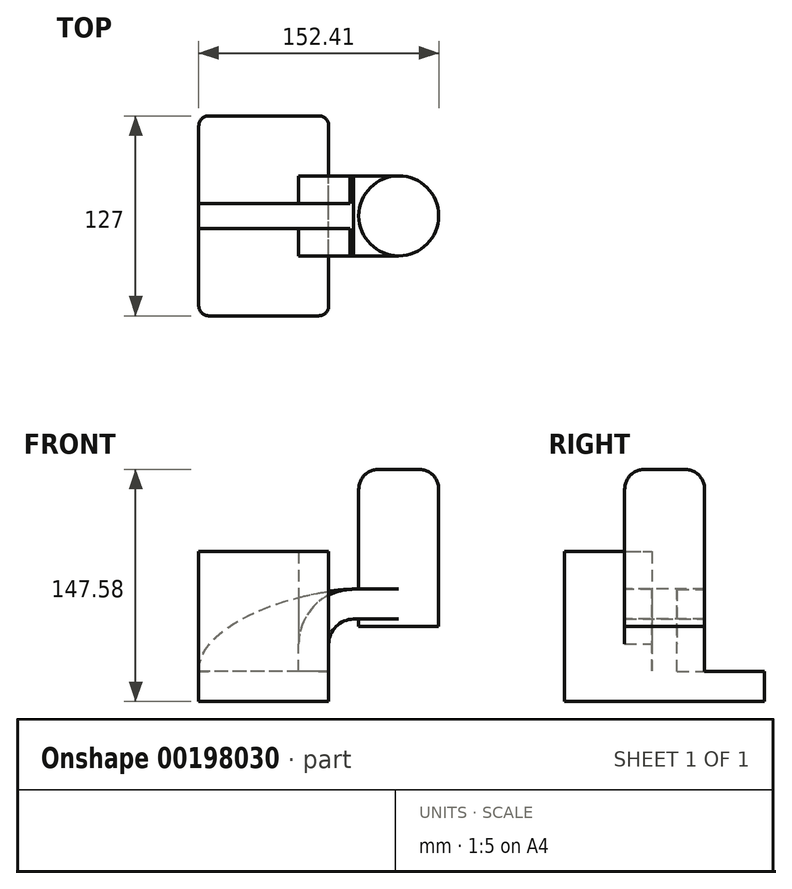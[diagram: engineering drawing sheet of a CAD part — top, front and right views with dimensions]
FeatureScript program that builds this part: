
annotation { "Feature Type Name" : "Feature", "Feature Type Description" : "" }
export const myFeature = defineFeature(function(context is Context, id is Id, definition is map)
    precondition{}
    {
        {
            var Q0;
            Q0=qCreatedBy(makeId("Front.planeOp"),FACE);
            var sketch = newSketch(context, id + "F0", { "sketchPlane" : qUnion([Q0])});
            skLineSegment(sketch, "E0.bottom", {"start": v(41.28, 9.53) * mm, "end": v(-41.28, 9.53) * mm});
            skLineSegment(sketch, "E0.top", {"start": v(41.28, -9.53) * mm, "end": v(-41.28, -9.53) * mm});
            skLineSegment(sketch, "E0.left", {"start": v(41.28, 9.53) * mm, "end": v(41.28, -9.53) * mm});
            skLineSegment(sketch, "E0.right", {"start": v(-41.28, 9.53) * mm, "end": v(-41.28, -9.53) * mm});
            skPoint(sketch, "E0.middle", {"position": v(0, 0) * mm});
            skLineSegment(sketch, "E1", {"start": v(41.28, 9.53) * mm, "end": v(41.28, 27) * mm});
            skArc(sketch, "E2", {"start": v(41.27, 27) * mm, "mid": v(45.92, 38.23) * mm, "end": v(57.15, 42.88) * mm});
            skLineSegment(sketch, "E3.bottom", {"start": v(60.32, 38.1) * mm, "end": v(111.12, 38.1) * mm});
            skLineSegment(sketch, "E3.top", {"start": v(60.32, 66.68) * mm, "end": v(111.12, 66.68) * mm});
            skLineSegment(sketch, "E3.left", {"start": v(60.32, 38.1) * mm, "end": v(60.32, 66.68) * mm});
            skLineSegment(sketch, "E3.right", {"start": v(111.12, 38.1) * mm, "end": v(111.12, 66.68) * mm});
            skPoint(sketch, "E3.middle", {"position": v(85.72, 52.39) * mm});
            skLineSegment(sketch, "E4", {"start": v(57.15, 42.88) * mm, "end": v(85.72, 42.88) * mm});
            skLineSegment(sketch, "E5.0", {"start": v(57.15, 61.93) * mm, "end": v(85.72, 61.93) * mm});
            skArc(sketch, "E5.1", {"start": v(22.22, 27) * mm, "mid": v(32.45, 51.7) * mm, "end": v(57.15, 61.93) * mm});
            skLineSegment(sketch, "E5.2", {"start": v(22.22, 9.53) * mm, "end": v(22.22, 27) * mm});
            skLineSegment(sketch, "E6", {"start": v(85.72, 66.68) * mm, "end": v(85.72, 38.1) * mm});
            skFitSpline(sketch, "E7", {"points": [v(-41.28, 9.52) * mm, v(57.15, 61.93) * mm], "startDerivative": vector(-0.84, 96.15) * mm, "endDerivative": vector(99.9, 2.09) * mm});
            skSolve(sketch);
        }
        {
            var Q0;
            Q0=makeQuery(id+"F0.imprint","IMPRINT",FACE,{"disambiguationData":[TD([[makeQuery(id+"F0.imprint","IMPRINT",EDGE,{"derivedFrom":sQuery(id+"F0.wireOp",EDGE,"E0.top")}),-1.0]])]});
            extrude(context, id + "F1", {"entities" : qUnion([Q0]), "endBound" : BoundingType.SYMMETRIC, "depth" : 127 * mm});
        }
        {
            var Q0;
            {var subQ5=sQuery(id+"F0.wireOp",EDGE,"E1");Q0=makeQuery(id+"F0.imprint","IMPRINT",FACE,{"disambiguationData":[TD([[makeQuery(id+"F0.imprint","IMPRINT",EDGE,{"derivedFrom":subQ5}),1.0]])]});}
            var Q1;
            {var subQ0=sQuery(id+"F0.wireOp",EDGE,"E4");var subQ1=sQuery(id+"F0.wireOp",EDGE,"E3.left");var subQ2=makeQuery(id+"F0.imprint","INTERSECT",VERTEX,{"derivedFrom":[subQ1,subQ0]});Q1=makeQuery(id+"F0.imprint","IMPRINT",FACE,{"disambiguationData":[TD([[makeQuery(id+"F0.imprint","IMPRINT",EDGE,{"disambiguationData":[TD([[subQ2,-1.0]])],"derivedFrom":subQ1}),-1.0]])]});}
            extrude(context, id + "F2", {"entities" : qUnion([Q0, Q1]), "operationType" : NewBodyOperationType.ADD, "endBound" : BoundingType.SYMMETRIC, "depth" : 50.8 * mm});
        }
        {
            var Q0;
            {var subQ3=sQuery(id+"F0.wireOp",EDGE,"E5.2");Q0=makeQuery(id+"F0.imprint","IMPRINT",FACE,{"disambiguationData":[TD([[makeQuery(id+"F0.imprint","IMPRINT",EDGE,{"derivedFrom":subQ3}),1.0]])]});}
            extrude(context, id + "F3", {"entities" : qUnion([Q0]), "operationType" : NewBodyOperationType.ADD, "endBound" : BoundingType.SYMMETRIC, "depth" : 15.88 * mm});
        }
        {
            var Q0;
            {var subQ5=sQuery(id+"F0.wireOp",EDGE,"E3.right");Q0=makeQuery(id+"F0.imprint","IMPRINT",FACE,{"disambiguationData":[TD([[makeQuery(id+"F0.imprint","IMPRINT",EDGE,{"derivedFrom":subQ5}),1.0]])]});}
            var Q1;
            Q1=sQuery(id+"F0.wireOp",EDGE,"E6");
            revolve(context, id + "F4", {"operationType" : NewBodyOperationType.ADD, "entities" : qUnion([Q0]), "axis" : qUnion([Q1]), "revolveType" : RevolveType.FULL});
        }
        {
            var Q0;
            Q0=makeQuery(id+"F1.opExtrude","CAP_EDGE",EDGE,{"disambiguationData":[OSD([sQuery(id+"F0.wireOp",EDGE,"E0.left")])],"isStart":false});
            var Q1;
            Q1=makeQuery(id+"F1.opExtrude","CAP_EDGE",EDGE,{"disambiguationData":[OSD([sQuery(id+"F0.wireOp",EDGE,"E0.right")])],"isStart":false});
            var Q2;
            Q2=makeQuery(id+"F1.opExtrude","CAP_EDGE",EDGE,{"disambiguationData":[OSD([sQuery(id+"F0.wireOp",EDGE,"E0.left")])],"isStart":true});
            var Q3;
            Q3=makeQuery(id+"F1.opExtrude","CAP_EDGE",EDGE,{"disambiguationData":[OSD([sQuery(id+"F0.wireOp",EDGE,"E0.right")])],"isStart":true});
            fillet(context, id + "F5", {"entities" : qUnion([Q0, Q1, Q2, Q3]), "radius" : 6.35 * mm, "tangentPropagation" : true, "allowEdgeOverflow" : false});
        }
        {
            var Q0;
            Q0=makeQuery(id+"F4.opRevolve","SWEPT_FACE",FACE,{"disambiguationData":[OSD([sQuery(id+"F0.wireOp",EDGE,"E3.top")])]});
            extrude(context, id + "F6", {"entities" : qUnion([Q0]), "operationType" : NewBodyOperationType.ADD, "depth" : 71.37 * mm});
        }
        {
            var Q0;
            {var subQ4=sQuery(id+"F0.wireOp",EDGE,"E0.bottom");var subQ5=sQuery(id+"F0.wireOp",EDGE,"E0.right");var subQ6=sQuery(id+"F0.wireOp",EDGE,"E0.left");Q0=makeQuery(id+"F3.boolean.opBoolean","SPLIT",FACE,{"disambiguationData":[TD([makeQuery(id+"F1.opExtrude","CAP_FACE",FACE,{"disambiguationData":[OSD([subQ4,sQuery(id+"F0.wireOp",EDGE,"E0.top"),subQ6,subQ5])],"isStart":false})])],"derivedFrom":makeQuery(id+"F1.opExtrude","SWEPT_FACE",FACE,{"disambiguationData":[OSD([subQ4])]})});}
            extrude(context, id + "F7", {"entities" : qUnion([Q0]), "operationType" : NewBodyOperationType.ADD, "depth" : 76.2 * mm});
        }
        {
            var Q0;
            Q0=makeQuery(id+"F6.opExtrude","CAP_EDGE",EDGE,{"disambiguationData":[OSD([sQuery(id+"F0.wireOp",EDGE,"E3.top"),sQuery(id+"F0.wireOp",EDGE,"E3.right")])],"isStart":false});
            fillet(context, id + "F8", {"entities" : qUnion([Q0]), "radius" : 12.7 * mm, "tangentPropagation" : true, "allowEdgeOverflow" : false});
        }
    });
